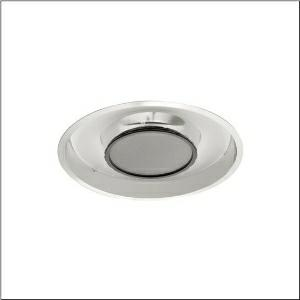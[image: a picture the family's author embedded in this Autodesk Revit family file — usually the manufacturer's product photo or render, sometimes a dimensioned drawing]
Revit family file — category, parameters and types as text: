
# Revit family: lunis_11_r_5lr610d4ob11af
name_source: partatom
category: Lighting Fixtures
units: mm (PartAtom-declared; Revit-internal decimal feet)

## family parameters
Cut with Voids When Loaded = No
Host = Face
Light Source = No
Part Type = Normal
Room Calculation Point = No
Round Connector Dimension = Use Diameter
Shared = No

## types (1)
- --- (1 x LED 4000K / CRI = 80 (unbekannt), 4860 lm, 4000K)
    Apparent Load = 37 VA
    CIE Flux Codes = 60 90 99 100 100
    Color Rendering = 80
    Color Temperature = 4000K
    Default Elevation = 1800 mm
    Description = Lunis 11 R, downlight, light control with reflector, of ultra-pure aluminium (Al 99.98%), highly specular, perforated, light emission: direct distribution, LED rated luminous flux: 4.860lm, light colour: 840, control gear: ECG Multilumen, with terminal, 3+2-pole, max. 2.5mm², mains connection: 230V, AC, 50/60Hz, diameter: 398mm, central ring, of plastic, graphite (RAL 7037), central module, blanking cover, of sheet steel, perforated, metallic grey (RAL 9006), protection rating (complete): IP20, insulation class (complete): insulation class II (safety insulation), certification: CE, ENEC, VDE, protection symbol: F, permissible ambient temperature for indoor applications: +10..+35°C, standard: EN 50419, packaging unit: 1 piece
    Height = 0 mm  [stored 0 ft]
    Lamp = 1 x LED 4000K / CRI >= 80 (unbekannt)
    Lamp Light Flux = 4860 lm
    Lamp count = 1
    Length = 398 mm
    Luminous efficacy = 131 lm/W
    Manufacturer = Siteco
    ModVariant = No
    Model = 5LR610D4OB11AF
    Mounting Place = Ceiling
    Mounting Type = Recessed
    Number of Poles = 1
    OnlyDefault = Yes
    Power Factor = 1
    Product Name = Lunis 11 R
    Product group = downlight | ceiling recessed
    ProductGroupID = 402
    Protection Class = Protection class II
    Protection Degree = IP 20
    RLX_Detail_Level = 1
    RlxData = <blob elided: 94417 chars, md5=b0a2eb11>
    Socket = socket
    Standby Power = 0 W
    System Light Flux = 4860 lm
    System Power = 37 W
    Type Comments = factory setting: High Lumen Output
    Type Image = l_1003323.jpg
    URL = http://relux.com
    VarID = @adj_145787
    Voltage = 0 V
    Weight = 0.00 kg
    Width = 0 mm  [stored 0 ft]

note: [stored X ft] marks values corroborated as IEEE doubles in the binary element streams (Revit-internal decimal feet)

## geometry (parser evidence)
native form markers: Blend x4, Sweep x12
no freeform markers — native parametric forms only
